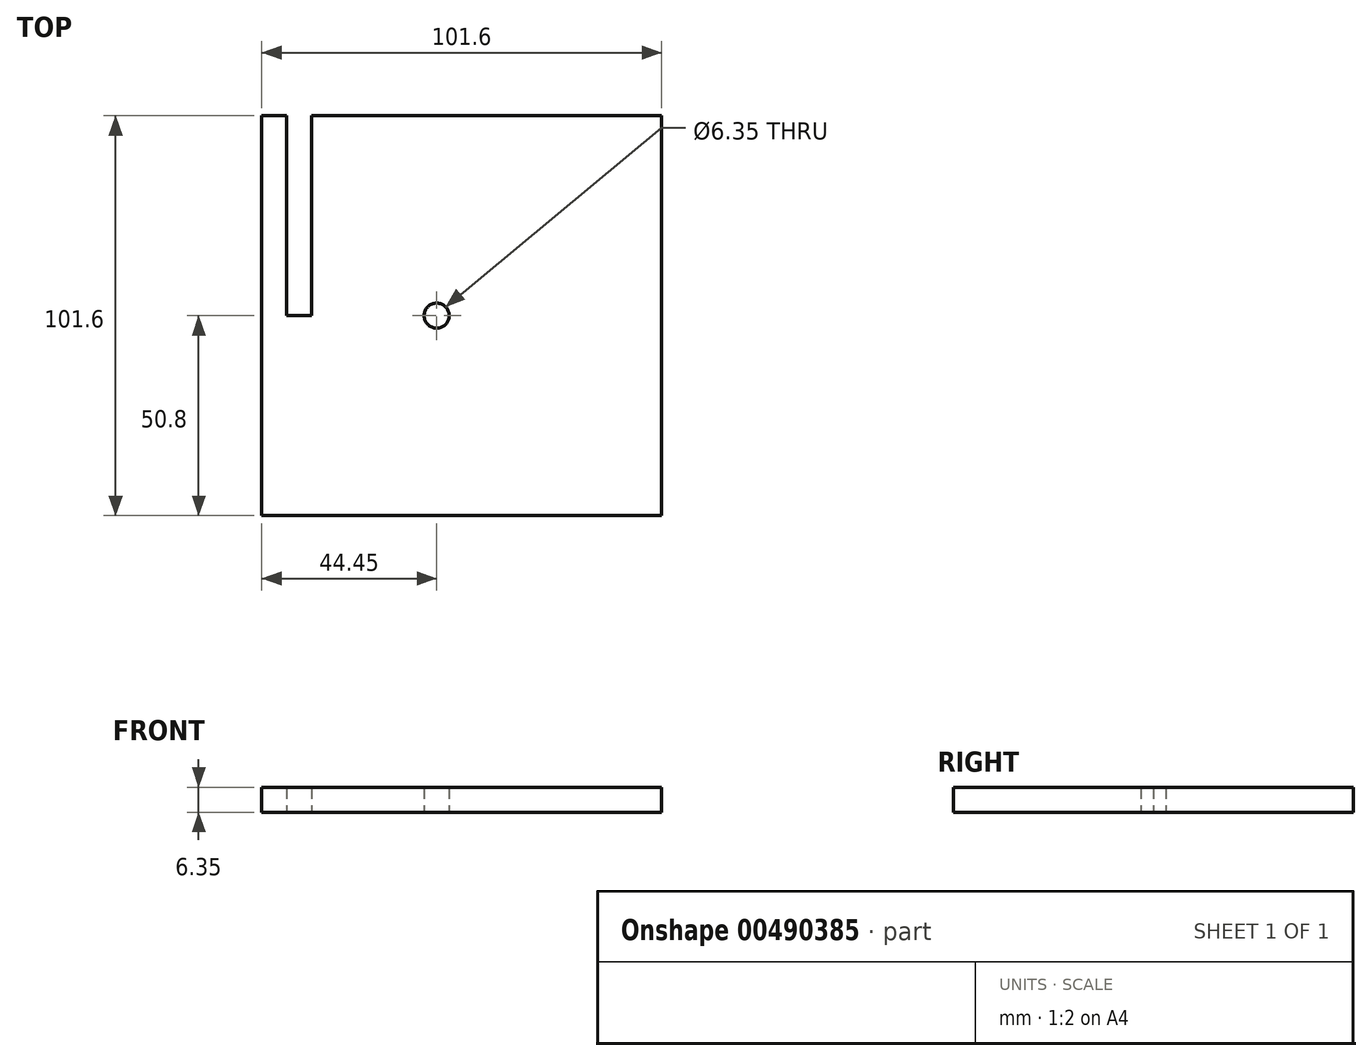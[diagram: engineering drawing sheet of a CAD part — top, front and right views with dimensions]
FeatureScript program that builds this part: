
annotation { "Feature Type Name" : "Feature", "Feature Type Description" : "" }
export const myFeature = defineFeature(function(context is Context, id is Id, definition is map)
    precondition{}
    {
        {
            var Q0;
            Q0=qCreatedBy(makeId("Top.planeOp"),FACE);
            var sketch = newSketch(context, id + "F0", { "sketchPlane" : qUnion([Q0])});
            skLineSegment(sketch, "E0.bottom", {"start": v(50.8, 50.8) * mm, "end": v(-50.8, 50.8) * mm});
            skLineSegment(sketch, "E0.top", {"start": v(50.8, -50.8) * mm, "end": v(-50.8, -50.8) * mm});
            skLineSegment(sketch, "E0.left", {"start": v(50.8, 50.8) * mm, "end": v(50.8, -50.8) * mm});
            skLineSegment(sketch, "E0.right", {"start": v(-50.8, 50.8) * mm, "end": v(-50.8, -50.8) * mm});
            skPoint(sketch, "E0.middle", {"position": v(0, 0) * mm});
            skSolve(sketch);
        }
        {
            var Q0;
            Q0 = qSketchRegion(id + "F0", true);
            extrude(context, id + "F1", {"entities" : qUnion([Q0]), "depth" : 6.35 * mm});
        }
        {
            var Q0;
            Q0=qCreatedBy(makeId("Top.planeOp"),FACE);
            var sketch = newSketch(context, id + "F2", { "sketchPlane" : qUnion([Q0])});
            skCircle(sketch, "E1", {"center": v(-6.35, 0) * mm, "radius": 3.18 * mm});
            skSolve(sketch);
        }
        {
            var Q0;
            Q0 = qSketchRegion(id + "F2", true);
            extrude(context, id + "F3", {"entities" : qUnion([Q0]), "operationType" : NewBodyOperationType.REMOVE, "endBound" : BoundingType.THROUGH_ALL, "depth" : 6.35 * mm});
        }
        {
            var Q0;
            Q0=qCreatedBy(makeId("Top.planeOp"),FACE);
            var sketch = newSketch(context, id + "F4", { "sketchPlane" : qUnion([Q0])});
            skLineSegment(sketch, "E2.bottom", {"start": v(-44.45, 50.8) * mm, "end": v(-38.1, 50.8) * mm});
            skLineSegment(sketch, "E2.top", {"start": v(-44.45, 0) * mm, "end": v(-38.1, 0) * mm});
            skLineSegment(sketch, "E2.left", {"start": v(-44.45, 50.8) * mm, "end": v(-44.45, 0) * mm});
            skLineSegment(sketch, "E2.right", {"start": v(-38.1, 50.8) * mm, "end": v(-38.1, 0) * mm});
            skSolve(sketch);
        }
        {
            var Q0;
            Q0 = qSketchRegion(id + "F4", true);
            extrude(context, id + "F5", {"entities" : qUnion([Q0]), "operationType" : NewBodyOperationType.REMOVE, "endBound" : BoundingType.THROUGH_ALL, "depth" : 29.97 * mm});
        }
    });
